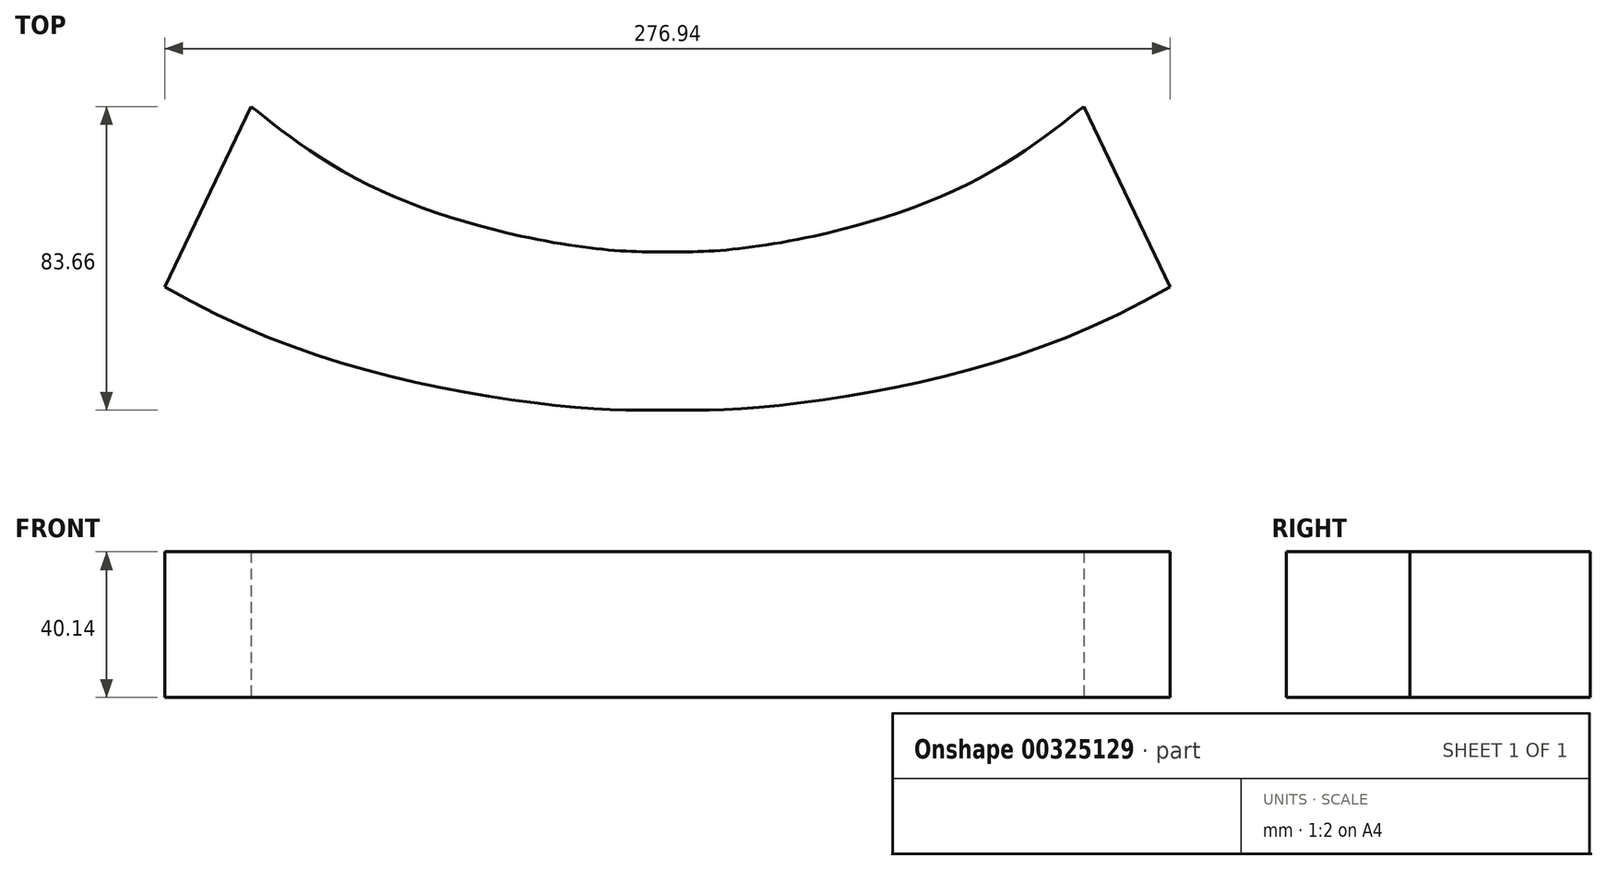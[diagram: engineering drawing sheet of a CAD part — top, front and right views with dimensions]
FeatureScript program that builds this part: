
annotation { "Feature Type Name" : "Feature", "Feature Type Description" : "" }
export const myFeature = defineFeature(function(context is Context, id is Id, definition is map)
    precondition{}
    {
        {
            var Q0;
            Q0=qCreatedBy(makeId("Top.planeOp"),FACE);
            var sketch = newSketch(context, id + "F0", { "sketchPlane" : qUnion([Q0])});
            skLineSegment(sketch, "E0", {"start": v(0, 961.12) * mm, "end": v(0, -258.08) * mm, "construction": true});
            skLineSegment(sketch, "E1", {"start": v(-40.36, 27.74) * mm, "end": v(-28.8, 862.36) * mm});
            skFitSpline(sketch, "E2", {"points": [v(0, 961.12) * mm, v(-17.81, 920.96) * mm, v(-28.8, 862.36) * mm], "startDerivative": vector(-46.68, -97.2) * mm, "endDerivative": vector(-3.38, -94.75) * mm});
            skLineSegment(sketch, "E3", {"start": v(-40.36, 27.74) * mm, "end": v(-40.74, 0) * mm});
            skLineSegment(sketch, "E4", {"start": v(-40.74, 0) * mm, "end": v(0, 0) * mm});
            skFitSpline(sketch, "E5.MirrorCS", {"points": [v(0, 961.12) * mm, v(17.81, 920.96) * mm, v(28.8, 862.36) * mm], "startDerivative": vector(46.68, -97.2) * mm, "endDerivative": vector(3.38, -94.75) * mm});
            skLineSegment(sketch, "E6.MirrorCS", {"start": v(40.36, 27.74) * mm, "end": v(28.8, 862.36) * mm});
            skLineSegment(sketch, "E7.MirrorCS", {"start": v(40.74, 0) * mm, "end": v(0, 0) * mm});
            skLineSegment(sketch, "E8.MirrorCS", {"start": v(40.36, 27.74) * mm, "end": v(40.74, 0) * mm});
            skLineSegment(sketch, "E9", {"start": v(-40.36, 27.74) * mm, "end": v(40.36, 27.74) * mm});
            skLineSegment(sketch, "E10", {"start": v(-138.47, 13.33) * mm, "end": v(-114.64, 63.02) * mm});
            skFitSpline(sketch, "E11", {"points": [v(-114.64, 63.02) * mm, v(-80.82, 40.68) * mm, v(-24.76, 24.5) * mm, v(0, 22.9) * mm], "startDerivative": vector(64.6, -51.6) * mm, "endDerivative": vector(82.51, -0.28) * mm});
            skFitSpline(sketch, "E12", {"points": [v(-138.47, 13.33) * mm, v(-72.3, -12.26) * mm, v(-21.78, -20.11) * mm, v(0, -20.63) * mm], "startDerivative": vector(168.1, -96.13) * mm, "endDerivative": vector(84.9, 0.11) * mm});
            skFitSpline(sketch, "E13.MirrorCS", {"points": [v(114.64, 63.02) * mm, v(80.82, 40.68) * mm, v(24.76, 24.5) * mm, v(0, 22.9) * mm], "startDerivative": vector(-64.6, -51.6) * mm, "endDerivative": vector(-82.51, -0.28) * mm});
            skLineSegment(sketch, "E14.MirrorCS", {"start": v(138.47, 13.33) * mm, "end": v(114.64, 63.02) * mm});
            skFitSpline(sketch, "E15.MirrorCS", {"points": [v(138.47, 13.33) * mm, v(72.3, -12.26) * mm, v(21.78, -20.11) * mm, v(0, -20.63) * mm], "startDerivative": vector(-168.1, -96.13) * mm, "endDerivative": vector(-84.9, 0.11) * mm});
            skSolve(sketch);
        }
        {
            var Q0;
            {var subQ4=sQuery(id+"F0.wireOp",EDGE,"E4");Q0=makeQuery(id+"F0.imprint","IMPRINT",FACE,{"disambiguationData":[TD([[makeQuery(id+"F0.imprint","IMPRINT",EDGE,{"derivedFrom":subQ4}),-1.0]])]});}
            var Q1;
            {var subQ4=sQuery(id+"F0.wireOp",EDGE,"E4");Q1=makeQuery(id+"F0.imprint","IMPRINT",FACE,{"disambiguationData":[TD([[makeQuery(id+"F0.imprint","IMPRINT",EDGE,{"derivedFrom":subQ4}),1.0]])]});}
            extrude(context, id + "F1", {"entities" : qUnion([Q0, Q1]), "depth" : 40.13 * mm, "symmetric" : true});
        }
    });
